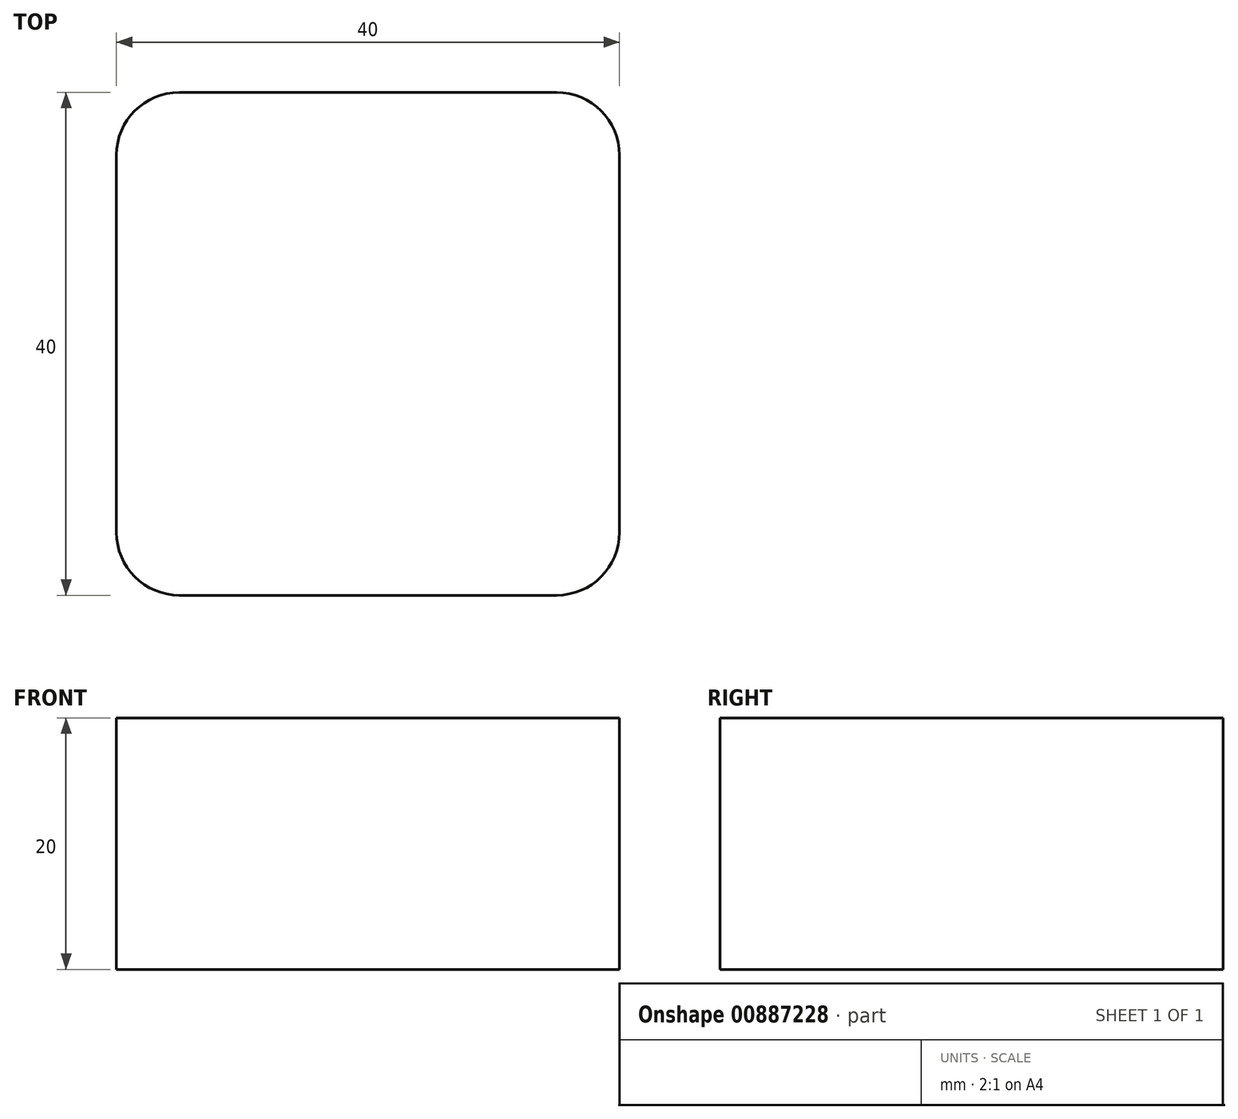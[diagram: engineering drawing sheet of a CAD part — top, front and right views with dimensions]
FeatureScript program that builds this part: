
annotation { "Feature Type Name" : "Feature", "Feature Type Description" : "" }
export const myFeature = defineFeature(function(context is Context, id is Id, definition is map)
    precondition{}
    {
        {
            var Q0;
            Q0=qCreatedBy(makeId("Top.planeOp"), FACE);
            var sketch = newSketch(context, id + "F0", { "sketchPlane" : qUnion([Q0])});
            skLineSegment(sketch, "E0.bottom", {"start": v(15, -20) * mm, "end": v(-15, -20) * mm});
            skLineSegment(sketch, "E0.top", {"start": v(15, 20) * mm, "end": v(-15, 20) * mm});
            skLineSegment(sketch, "E0.left", {"start": v(20, -15) * mm, "end": v(20, 15) * mm});
            skLineSegment(sketch, "E0.right", {"start": v(-20, -15) * mm, "end": v(-20, 15) * mm});
            skPoint(sketch, "E0.middle", {"position": v(0, 0) * mm});
            skPoint(sketch, "E1.0.visualSharp", {"position": v(-20, 20) * mm});
            skArc(sketch, "E1.0.filletArc", {"start": v(-15, 20) * mm, "mid": v(-18.54, 18.54) * mm, "end": v(-20, 15) * mm});
            skPoint(sketch, "E1.1.visualSharp", {"position": v(-20, -20) * mm});
            skArc(sketch, "E1.1.filletArc", {"start": v(-20, -15) * mm, "mid": v(-18.54, -18.54) * mm, "end": v(-15, -20) * mm});
            skPoint(sketch, "E1.2.visualSharp", {"position": v(20, -20) * mm});
            skArc(sketch, "E1.2.filletArc", {"start": v(15, -20) * mm, "mid": v(18.54, -18.54) * mm, "end": v(20, -15) * mm});
            skPoint(sketch, "E1.3.visualSharp", {"position": v(20, 20) * mm});
            skArc(sketch, "E1.3.filletArc", {"start": v(20, 15) * mm, "mid": v(18.54, 18.54) * mm, "end": v(15, 20) * mm});
            skSolve(sketch);
        }
        {
            var Q0;
            Q0 = qSketchRegion(id + "F0", true);
            extrude(context, id + "F1", {"entities" : qUnion([Q0]), "domain" : OperationDomain.MODEL, "flatOperationType" : FlatOperationType.REMOVE, "depth" : 20 * mm, "offsetDistance" : 25 * mm});
        }
    });
